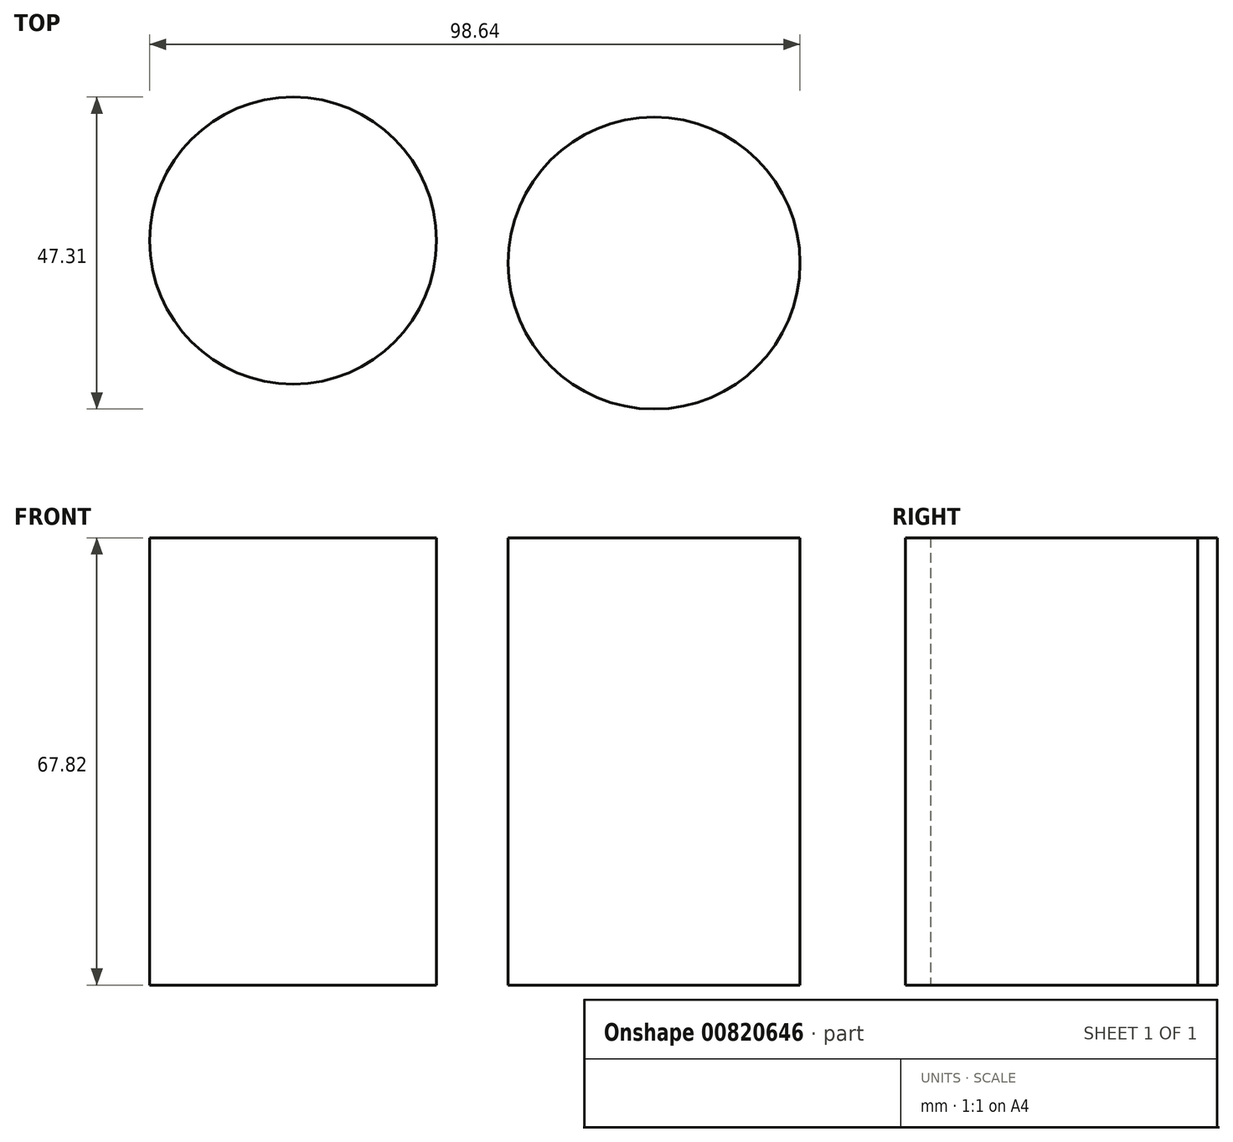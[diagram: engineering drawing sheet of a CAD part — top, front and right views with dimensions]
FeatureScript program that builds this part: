
annotation { "Feature Type Name" : "Feature", "Feature Type Description" : "" }
export const myFeature = defineFeature(function(context is Context, id is Id, definition is map)
    precondition{}
    {
        {
            var Q0;
            Q0=qCreatedBy(makeId("Top.planeOp"),FACE);
            var sketch = newSketch(context, id + "F0", { "sketchPlane" : qUnion([Q0])});
            skCircle(sketch, "E0", {"center": v(-26.27, 38.25) * mm, "radius": 21.75 * mm});
            skCircle(sketch, "E1", {"center": v(28.47, 34.83) * mm, "radius": 22.14 * mm});
            skSolve(sketch);
        }
        {
            var Q0;
            Q0=makeQuery(id+"F0.imprint","IMPRINT",FACE,{"disambiguationData":[TD([[makeQuery(id+"F0.imprint","IMPRINT",EDGE,{"derivedFrom":sQuery(id+"F0.wireOp",EDGE,"E0")}),1.0]])]});
            var Q1;
            Q1=makeQuery(id+"F0.imprint","IMPRINT",FACE,{"disambiguationData":[TD([[makeQuery(id+"F0.imprint","IMPRINT",EDGE,{"derivedFrom":sQuery(id+"F0.wireOp",EDGE,"E1")}),1.0]])]});
            extrude(context, id + "F1", {"entities" : qUnion([Q0, Q1]), "depth" : 67.82 * mm, "offsetDistance" : 25.4 * mm});
        }
    });
